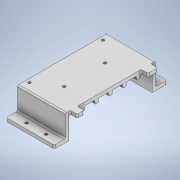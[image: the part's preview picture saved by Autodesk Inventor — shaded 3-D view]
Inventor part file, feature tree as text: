
AUTODESK INVENTOR PART (.ipt)
format: ipt  version: 2020 (Build 240168000, 168)  size: 325,120 bytes
history: native  units: in
note: dims shown in document units (in); Inventor stores cm internally (conversion verified against a paired STEP export)
features: extrude x5, sketch x5, fillet x4, hole x2, mirror x1, pattern_linear x1
ambient origin geometry x8: Origin, YZ Plane, XZ Plane, XY Plane, X Axis, Y Axis, Z Axis, Center Point
bodies: Solid1 (feature_tree)
feature tree (18):
  extrude  "Extrusion1"  Depth=4.7244in
  extrude  "Extrusion2"  Depth=6.378in
  extrude  "Extrusion3"  Depth=0.1969in TaperAngle=0.0deg
  hole  "Hole1"  [1 undecoded]
  mirror  "Mirror1"
  extrude  "Extrusion4"  Depth=0.0787in TaperAngle=0.0deg
  extrude  "Extrusion5"  Depth=0.0787in
  pattern_linear  "Rectangular Pattern1"  Spacing1=1.1024in  [1 undecoded]
  fillet  "Fillet1"  Radius=0.2953in
  fillet  "Fillet2"  Radius=0.2953in
  fillet  "Fillet3"  Radius=2.7244in
  fillet  "Fillet6"  Radius=4.5669in
  sketch  "Sketch1"  dims[d0=2.7244in d1=4.7244in]
  sketch  "Sketch3"  dims[d2=2.7244in d3=6.378in]
  sketch  "Sketch4"  dims[d4=0.7874in d5=0.1969in d6=0.0in]
  sketch  "Sketch5"  dims[d7=0.1969in d8=0.1969in]
  hole  "Hole Pattern"  [1 undecoded]
  sketch  "Sketch7"  dims[d9=1.2598in d10=0.0in d11=0.1969in d12=0.0in d13=0.7677in d14=1.1024in d15=0.2953in d16=0.2953in d17=0.1628in d18=0.3937in d19=0.1575in d20=0.0787in d21=90.0deg d22=0.5591in d23=0.8108in d24=2.7244in d25=4.5669in d26=0.1496in d27=0.1496in d29=0.1496in d30=0.1969in d31=2.5197in d32=0.9843in d33=1.3386in d34=3.3071in d35=1.3386in d36=4.3701in d37=2.5197in d38=0.1969in d39=0.0in d40=2.7244in d41=0.1969in d42=0.2165in d43=0.0in d44=1.1811in d46=0.7874in d47=1.1811in d49=0.7874in d50=0.0787in d51=0.0394in d52=0.0787in d53=0.3937in d54=0.4724in d55=0.3937in d56=0.6299in d59=0.3937in d60=0.3937in d61=0.3937in d62=0.5512in d63=0.0787in d71=0.2756in d72=0.1969in d73=0.1969in d74=0.1969in d75=0.1496in d76=0.1496in d77=0.1969in d78=0.1969in d79=0.2756in d80=0.1969in d81=0.1496in]
note: 3 required parameter values undecoded (feature->parameter linkage not recoverable at this tier; creation-order binding heuristic only, values carry confidence <= 0.55)
